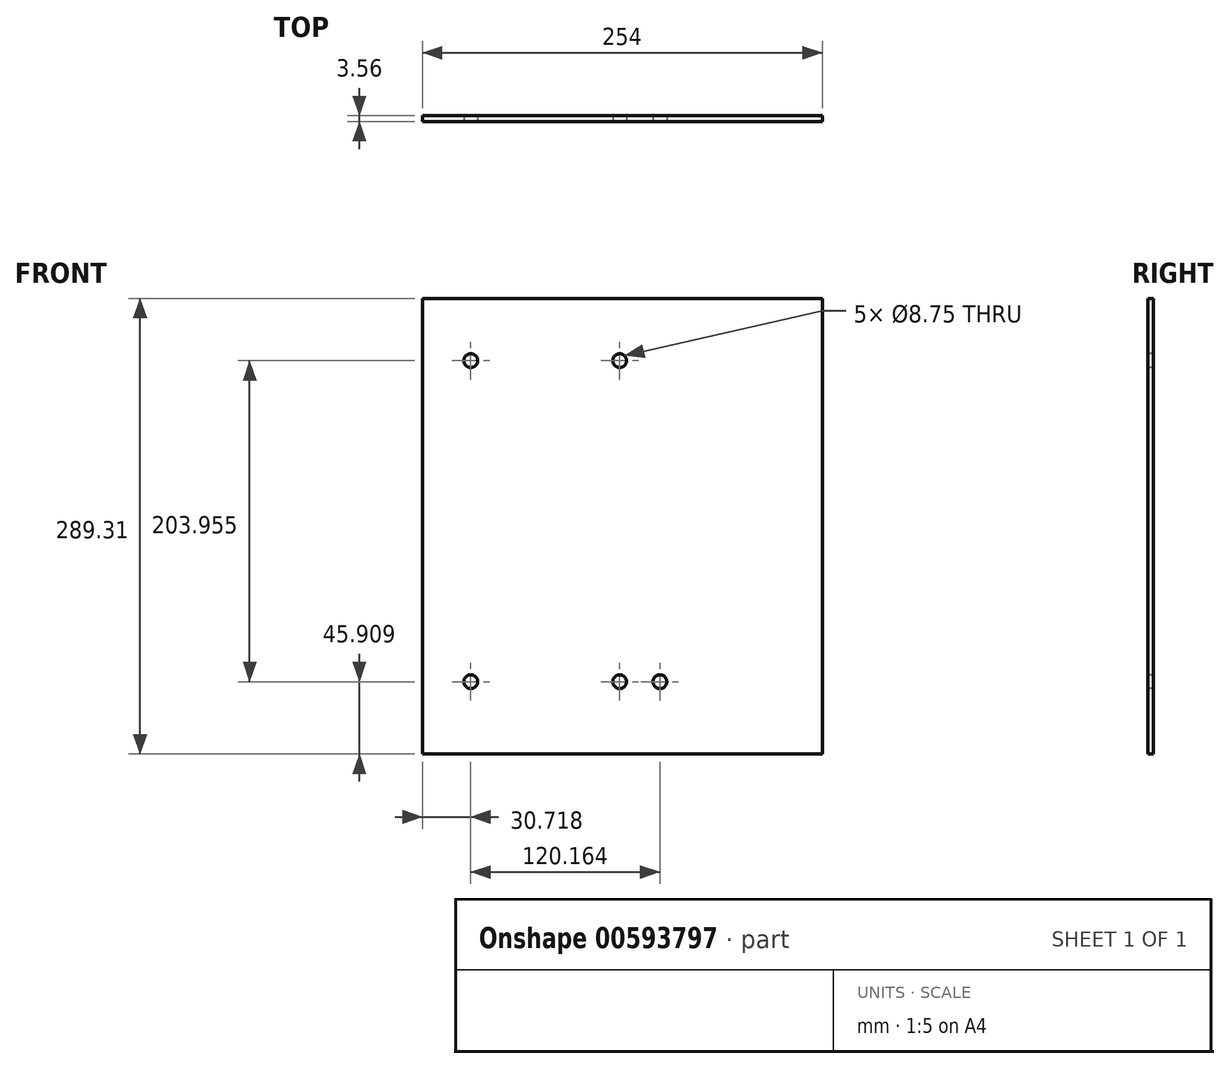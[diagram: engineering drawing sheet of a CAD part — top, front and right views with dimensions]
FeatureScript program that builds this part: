
annotation { "Feature Type Name" : "Feature", "Feature Type Description" : "" }
export const myFeature = defineFeature(function(context is Context, id is Id, definition is map)
    precondition{}
    {
        {
            var Q0;
            Q0=qCreatedBy(makeId("Front.planeOp"),FACE);
            var sketch = newSketch(context, id + "F0", { "sketchPlane" : qUnion([Q0])});
            skLineSegment(sketch, "E0.bottom", {"start": v(-59.11, 248.35) * mm, "end": v(194.89, 248.35) * mm});
            skLineSegment(sketch, "E0.top", {"start": v(-59.11, -40.96) * mm, "end": v(194.89, -40.96) * mm});
            skLineSegment(sketch, "E0.left", {"start": v(-59.11, 248.35) * mm, "end": v(-59.11, -40.96) * mm});
            skLineSegment(sketch, "E0.right", {"start": v(194.89, 248.35) * mm, "end": v(194.89, -40.96) * mm});
            skSolve(sketch);
        }
        {
            var Q0;
            Q0=makeQuery(id+"F0.imprint","IMPRINT",FACE,{"disambiguationData":[TD([[makeQuery(id+"F0.imprint","IMPRINT",EDGE,{"derivedFrom":sQuery(id+"F0.wireOp",EDGE,"E0.bottom")}),-1.0]])]});
            extrude(context, id + "F1", {"entities" : qUnion([Q0]), "depth" : 3.56 * mm, "offsetDistance" : 25.4 * mm});
        }
        {
            var Q0;
            Q0=makeQuery(id+"F1.opExtrude","CAP_FACE",FACE,{"disambiguationData":[OSD([sQuery(id+"F0.wireOp",EDGE,"E0.bottom"),sQuery(id+"F0.wireOp",EDGE,"E0.top"),sQuery(id+"F0.wireOp",EDGE,"E0.left"),sQuery(id+"F0.wireOp",EDGE,"E0.right")])],"isStart":false});
            var sketch = newSketch(context, id + "F2", { "sketchPlane" : qUnion([Q0])});
            skCircle(sketch, "E1", {"center": v(-28.4, 4.95) * mm, "radius": 4.38 * mm});
            skCircle(sketch, "E2", {"center": v(-28.4, 208.9) * mm, "radius": 4.38 * mm});
            skCircle(sketch, "E3", {"center": v(66.21, 4.95) * mm, "radius": 4.38 * mm});
            skCircle(sketch, "E4", {"center": v(66.21, 208.9) * mm, "radius": 4.38 * mm});
            skCircle(sketch, "E5", {"center": v(91.77, 4.95) * mm, "radius": 4.38 * mm});
            skSolve(sketch);
        }
        {
            var Q0;
            Q0=makeQuery(id+"F2.imprint","IMPRINT",FACE,{"disambiguationData":[TD([[makeQuery(id+"F2.imprint","IMPRINT",EDGE,{"derivedFrom":sQuery(id+"F2.wireOp",EDGE,"E1")}),1.0]])]});
            extrude(context, id + "F3", {"entities" : qUnion([Q0]), "operationType" : NewBodyOperationType.REMOVE, "oppositeDirection" : true, "depth" : 25.4 * mm, "offsetDistance" : 25.4 * mm});
        }
        {
            var Q0;
            Q0 = qSketchRegion(id + "F2", true);
            extrude(context, id + "F4", {"entities" : qUnion([Q0]), "operationType" : NewBodyOperationType.REMOVE, "oppositeDirection" : true, "depth" : 25.4 * mm, "offsetDistance" : 25.4 * mm});
        }
    });
